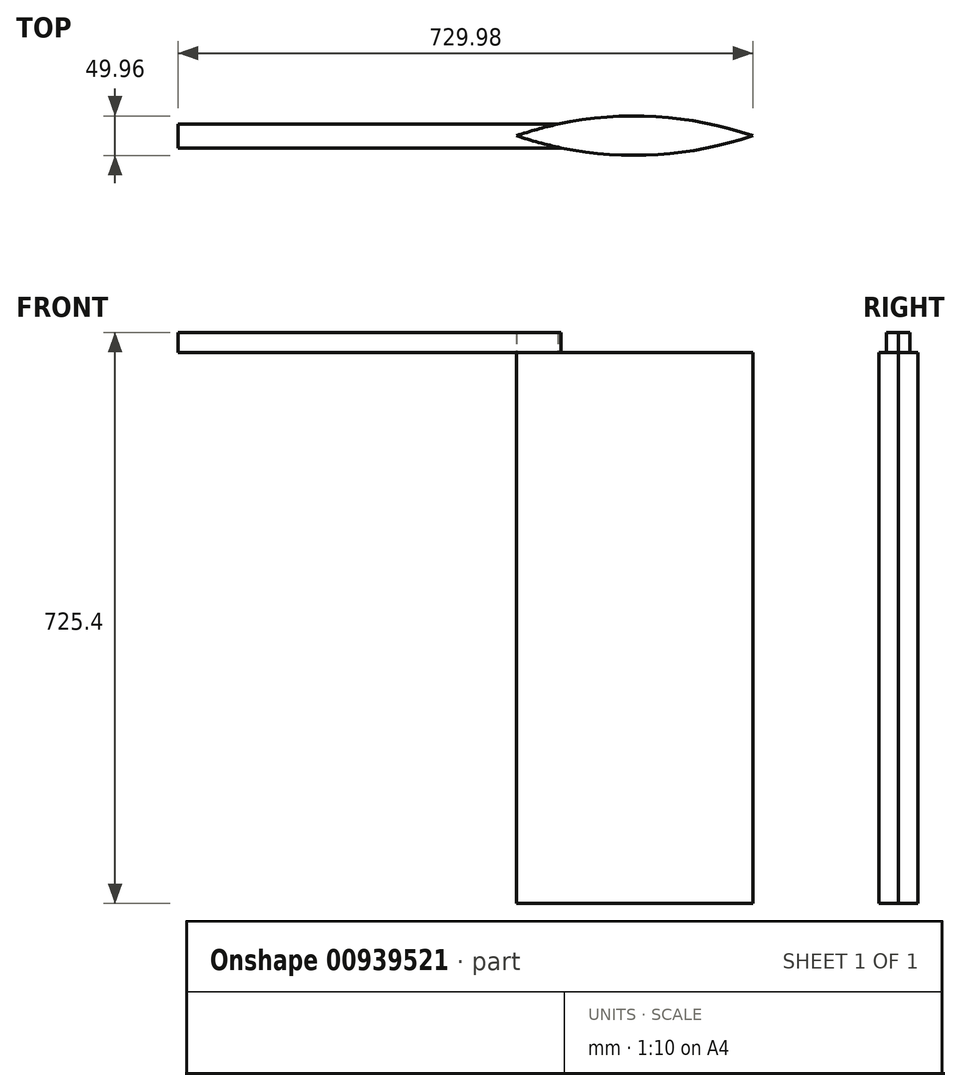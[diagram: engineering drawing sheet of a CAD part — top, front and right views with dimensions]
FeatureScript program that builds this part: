
annotation { "Feature Type Name" : "Feature", "Feature Type Description" : "" }
export const myFeature = defineFeature(function(context is Context, id is Id, definition is map)
    precondition{}
    {
        {
            var Q0;
            Q0=qCreatedBy(makeId("Top.planeOp"),FACE);
            var sketch = newSketch(context, id + "F0", { "sketchPlane" : qUnion([Q0])});
            skArc(sketch, "E0", {"start": v(300, 0) * mm, "mid": v(150, 24.98) * mm, "end": v(0, 0) * mm});
            skLineSegment(sketch, "E1", {"start": v(0, 0) * mm, "end": v(300, 0) * mm});
            skSolve(sketch);
        }
        {
            var Q0;
            Q0=makeQuery(id+"F0.imprint","IMPRINT",FACE,{"disambiguationData":[TD([[makeQuery(id+"F0.imprint","IMPRINT",EDGE,{"derivedFrom":sQuery(id+"F0.wireOp",EDGE,"E0")}),1.0]])]});
            extrude(context, id + "F1", {"entities" : qUnion([Q0]), "oppositeDirection" : true, "depth" : 700 * mm, "offsetDistance" : 25 * mm});
        }
        {
            var Q0;
            Q0=makeQuery(id+"F1.opExtrude","SWEPT_BODY",BODY,{"disambiguationData":[OSD([sQuery(id+"F0.wireOp",EDGE,"E0"),sQuery(id+"F0.wireOp",EDGE,"E1")])]});
            var Q1;
            Q1=qCreatedBy(makeId("Front.planeOp"),FACE);
            mirror(context, id + "F2", {"operationType" : NewBodyOperationType.ADD, "entities" : qUnion([Q0]), "mirrorPlane" : qUnion([Q1])});
        }
        {
            var Q0;
            {var subQ0=makeQuery(id+"F1.opExtrude","CAP_FACE",FACE,{"disambiguationData":[OSD([sQuery(id+"F0.wireOp",EDGE,"E0"),sQuery(id+"F0.wireOp",EDGE,"E1")])],"isStart":true});Q0=makeQuery(id+"F2.boolean.opBoolean","MERGE",FACE,{"derivedFrom":[subQ0,makeQuery(id+"F2.opPattern","COPY",FACE,{"derivedFrom":subQ0,"instanceName":"1"})]});}
            var sketch = newSketch(context, id + "F3", { "sketchPlane" : qUnion([Q0])});
            skLineSegment(sketch, "E2.bottom", {"start": v(70.02, 14.53) * mm, "end": v(-429.98, 14.53) * mm});
            skLineSegment(sketch, "E2.top", {"start": v(70.02, -15.47) * mm, "end": v(-429.98, -15.47) * mm});
            skLineSegment(sketch, "E2.left", {"start": v(70.02, 14.53) * mm, "end": v(70.02, -15.47) * mm});
            skLineSegment(sketch, "E2.right", {"start": v(-429.98, 14.53) * mm, "end": v(-429.98, -15.47) * mm});
            skSolve(sketch);
        }
        {
            var Q0;
            {var subQ5=sQuery(id+"F3.wireOp",EDGE,"E2.right");Q0=makeQuery(id+"F3.imprint","IMPRINT",FACE,{"disambiguationData":[TD([[makeQuery(id+"F3.imprint","IMPRINT",EDGE,{"derivedFrom":subQ5}),1.0]])]});}
            extrude(context, id + "F4", {"entities" : qUnion([Q0]), "depth" : 25.4 * mm, "offsetDistance" : 25 * mm});
        }
    });
